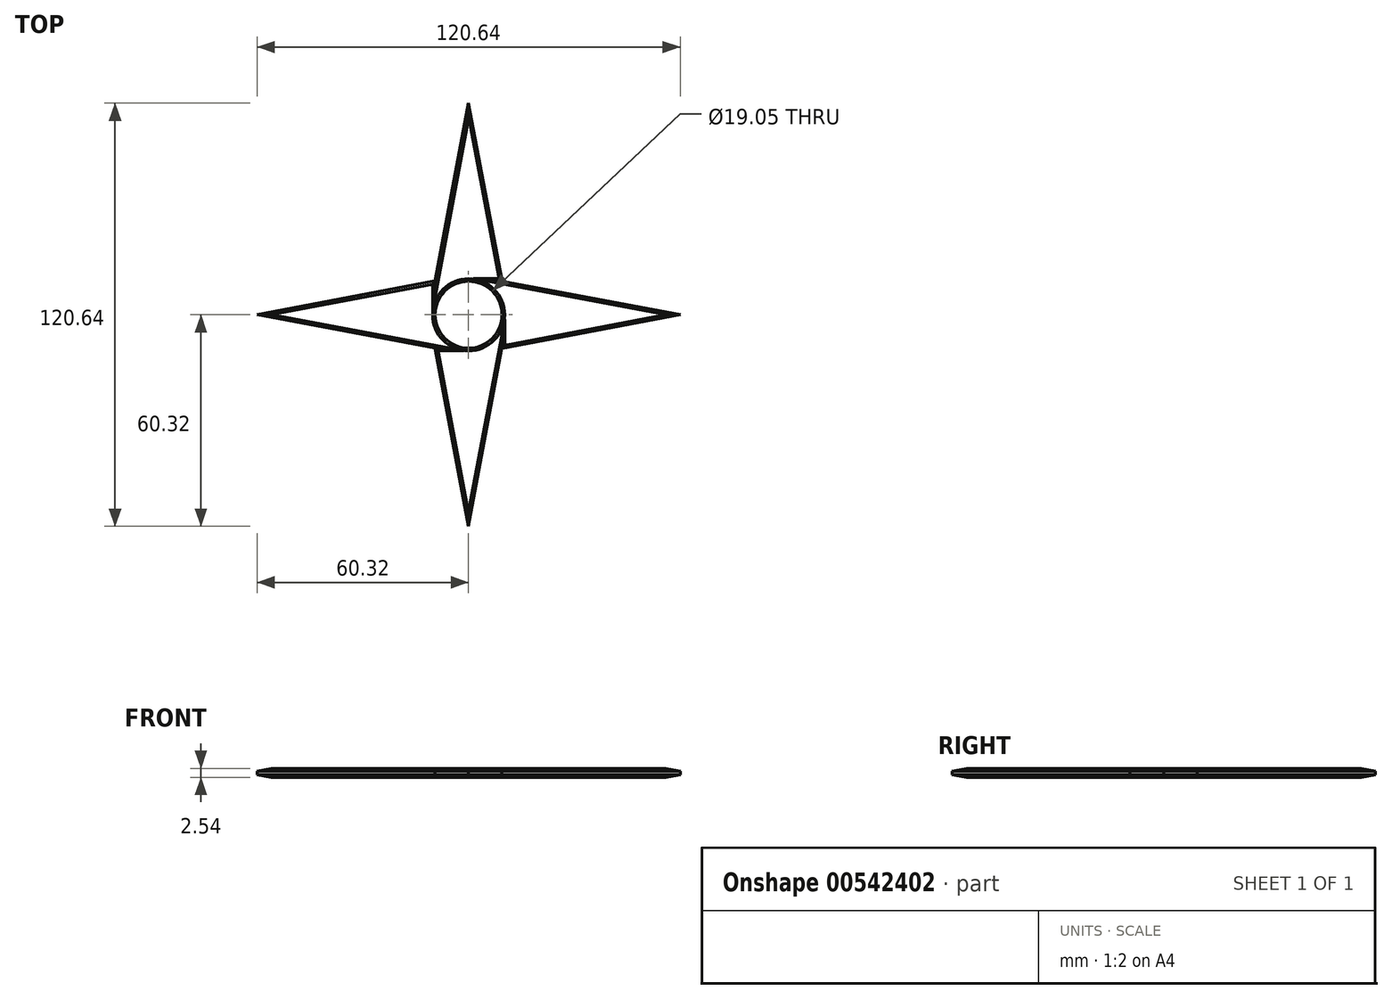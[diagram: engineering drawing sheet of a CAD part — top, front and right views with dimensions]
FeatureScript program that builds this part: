
annotation { "Feature Type Name" : "Feature", "Feature Type Description" : "" }
export const myFeature = defineFeature(function(context is Context, id is Id, definition is map)
    precondition{}
    {
        {
            var Q0;
            Q0=qCreatedBy(makeId("Top.planeOp"),FACE);
            var sketch = newSketch(context, id + "F0", { "sketchPlane" : qUnion([Q0])});
            skLineSegment(sketch, "E0.bottom", {"start": v(9.52, -9.52) * mm, "end": v(-9.52, -9.53) * mm});
            skLineSegment(sketch, "E0.top", {"start": v(9.52, 9.53) * mm, "end": v(-9.53, 9.52) * mm});
            skLineSegment(sketch, "E0.left", {"start": v(9.52, -9.52) * mm, "end": v(9.52, 9.53) * mm});
            skLineSegment(sketch, "E0.right", {"start": v(-9.52, -9.53) * mm, "end": v(-9.52, 9.52) * mm});
            skPoint(sketch, "E0.middle", {"position": v(0, 0) * mm});
            skSolve(sketch);
        }
        {
            var Q0;
            Q0 = qSketchRegion(id + "F0", true);
            extrude(context, id + "F1", {"entities" : qUnion([Q0]), "depth" : 2.54 * mm, "offsetDistance" : 25.4 * mm});
        }
        {
            var Q0;
            Q0=makeQuery(id+"F1.opExtrude","CAP_FACE",FACE,{"disambiguationData":[OSD([sQuery(id+"F0.wireOp",EDGE,"E0.bottom"),sQuery(id+"F0.wireOp",EDGE,"E0.top"),sQuery(id+"F0.wireOp",EDGE,"E0.left"),sQuery(id+"F0.wireOp",EDGE,"E0.right")])],"isStart":true});
            var sketch = newSketch(context, id + "F2", { "sketchPlane" : qUnion([Q0])});
            skCircle(sketch, "E1", {"center": v(0, 0) * mm, "radius": 9.53 * mm});
            skSolve(sketch);
        }
        {
            var Q0;
            {var subQ0=sQuery(id+"F0.wireOp",EDGE,"E0.top");var subQ1=sQuery(id+"F0.wireOp",EDGE,"E0.left");Q0=makeQuery(id+"F1ypjoiV6kp7A7C_1.boolean.opBoolean","SPLIT",FACE,{"disambiguationData":[TD([makeQuery(id+"F1.opExtrude","SWEPT_FACE",FACE,{"disambiguationData":[OSD([subQ0])]}),makeQuery(id+"F1.opExtrude","SWEPT_FACE",FACE,{"disambiguationData":[OSD([subQ1])]}),makeQuery(id+"F1ypjoiV6kp7A7C_1.opExtrude","SWEPT_FACE",FACE,{"disambiguationData":[OSD([sQuery(id+"F2.wireOp",EDGE,"E1")])]})])],"derivedFrom":makeQuery(id+"F1.opExtrude","CAP_FACE",FACE,{"disambiguationData":[OSD([sQuery(id+"F0.wireOp",EDGE,"E0.bottom"),subQ0,subQ1,sQuery(id+"F0.wireOp",EDGE,"E0.right")])],"isStart":true})});}
            var sketch = newSketch(context, id + "F3", { "sketchPlane" : qUnion([Q0])});
            skLineSegment(sketch, "E2", {"start": v(9.53, -9.52) * mm, "end": v(60.33, 0) * mm});
            skLineSegment(sketch, "E3", {"start": v(60.33, 0) * mm, "end": v(9.52, 9.63) * mm});
            skLineSegment(sketch, "E4", {"start": v(9.52, 9.63) * mm, "end": v(9.53, -9.52) * mm});
            skLineSegment(sketch, "E5.1.0", {"start": v(9.52, 9.53) * mm, "end": v(0, 60.33) * mm});
            skLineSegment(sketch, "E5.1.1", {"start": v(0, 60.33) * mm, "end": v(-9.63, 9.52) * mm});
            skLineSegment(sketch, "E5.1.2", {"start": v(-9.63, 9.52) * mm, "end": v(9.52, 9.53) * mm});
            skLineSegment(sketch, "E5.2.0", {"start": v(-9.53, 9.52) * mm, "end": v(-60.33, 0) * mm});
            skLineSegment(sketch, "E5.2.1", {"start": v(-60.33, 0) * mm, "end": v(-9.52, -9.63) * mm});
            skLineSegment(sketch, "E5.2.2", {"start": v(-9.53, -9.63) * mm, "end": v(-9.53, 9.53) * mm});
            skLineSegment(sketch, "E5.3.0", {"start": v(-9.52, -9.53) * mm, "end": v(0, -60.33) * mm});
            skLineSegment(sketch, "E5.3.1", {"start": v(0, -60.33) * mm, "end": v(9.63, -9.52) * mm});
            skLineSegment(sketch, "E5.3.2", {"start": v(9.63, -9.53) * mm, "end": v(-9.53, -9.53) * mm});
            skPoint(sketch, "E5.center", {"position": v(0, 0) * mm});
            skSolve(sketch);
        }
        {
            var Q0;
            Q0 = qSketchRegion(id + "F3", true);
            extrude(context, id + "F4", {"entities" : qUnion([Q0]), "operationType" : NewBodyOperationType.ADD, "depth" : -2.54 * mm, "offsetDistance" : 25.4 * mm});
        }
        {
            var Q0;
            {var subQ0=sQuery(id+"F2.wireOp",EDGE,"E1");var subQ1=makeQuery(id+"F2.imprint","INTERSECT",VERTEX,{"derivedFrom":[makeQuery(id+"F1.opExtrude","CAP_EDGE",EDGE,{"disambiguationData":[OSD([sQuery(id+"F0.wireOp",EDGE,"E0.bottom")])],"isStart":true}),subQ0]});Q0=makeQuery(id+"F2.imprint","IMPRINT",FACE,{"disambiguationData":[TD([[makeQuery(id+"F2.imprint","IMPRINT",EDGE,{"disambiguationData":[TD([[subQ1,1.0]])],"derivedFrom":subQ0}),1.0]])]});}
            extrude(context, id + "F5", {"entities" : qUnion([Q0]), "operationType" : NewBodyOperationType.REMOVE, "oppositeDirection" : true, "depth" : 25.4 * mm, "offsetDistance" : 25.4 * mm});
        }
        {
            var Q0;
            Q0=makeQuery(id+"F4.boolean.opBoolean","MERGE",FACE,{"derivedFrom":[makeQuery(id+"F1.opExtrude","CAP_FACE",FACE,{"disambiguationData":[OSD([sQuery(id+"F0.wireOp",EDGE,"E0.bottom"),sQuery(id+"F0.wireOp",EDGE,"E0.top"),sQuery(id+"F0.wireOp",EDGE,"E0.left"),sQuery(id+"F0.wireOp",EDGE,"E0.right")])],"isStart":false}),makeQuery(id+"F4.opExtrude","CAP_FACE",FACE,{"disambiguationData":[OSD([sQuery(id+"F3.wireOp",EDGE,"E2"),sQuery(id+"F3.wireOp",EDGE,"E3"),sQuery(id+"F3.wireOp",EDGE,"E4"),sQuery(id+"F3.wireOp",EDGE,"E5.1.0"),sQuery(id+"F3.wireOp",EDGE,"E5.1.1"),sQuery(id+"F3.wireOp",EDGE,"E5.1.2"),sQuery(id+"F3.wireOp",EDGE,"E5.2.0"),sQuery(id+"F3.wireOp",EDGE,"E5.2.1"),sQuery(id+"F3.wireOp",EDGE,"E5.2.2"),sQuery(id+"F3.wireOp",EDGE,"E5.3.0"),sQuery(id+"F3.wireOp",EDGE,"E5.3.1"),sQuery(id+"F3.wireOp",EDGE,"E5.3.2")])],"isStart":false})]});
            var Q1;
            Q1=makeQuery(id+"F4.boolean.opBoolean","MERGE",FACE,{"derivedFrom":[makeQuery(id+"F1.opExtrude","CAP_FACE",FACE,{"disambiguationData":[OSD([sQuery(id+"F0.wireOp",EDGE,"E0.bottom"),sQuery(id+"F0.wireOp",EDGE,"E0.top"),sQuery(id+"F0.wireOp",EDGE,"E0.left"),sQuery(id+"F0.wireOp",EDGE,"E0.right")])],"isStart":true}),makeQuery(id+"F4.opExtrude","CAP_FACE",FACE,{"disambiguationData":[OSD([sQuery(id+"F3.wireOp",EDGE,"E2"),sQuery(id+"F3.wireOp",EDGE,"E3"),sQuery(id+"F3.wireOp",EDGE,"E4"),sQuery(id+"F3.wireOp",EDGE,"E5.1.0"),sQuery(id+"F3.wireOp",EDGE,"E5.1.1"),sQuery(id+"F3.wireOp",EDGE,"E5.1.2"),sQuery(id+"F3.wireOp",EDGE,"E5.2.0"),sQuery(id+"F3.wireOp",EDGE,"E5.2.1"),sQuery(id+"F3.wireOp",EDGE,"E5.2.2"),sQuery(id+"F3.wireOp",EDGE,"E5.3.0"),sQuery(id+"F3.wireOp",EDGE,"E5.3.1"),sQuery(id+"F3.wireOp",EDGE,"E5.3.2")])],"isStart":true})]});
            chamfer(context, id + "F6", {"entities" : qUnion([Q0, Q1]), "width" : 0.76 * mm, "tangentPropagation" : true});
        }
    });
